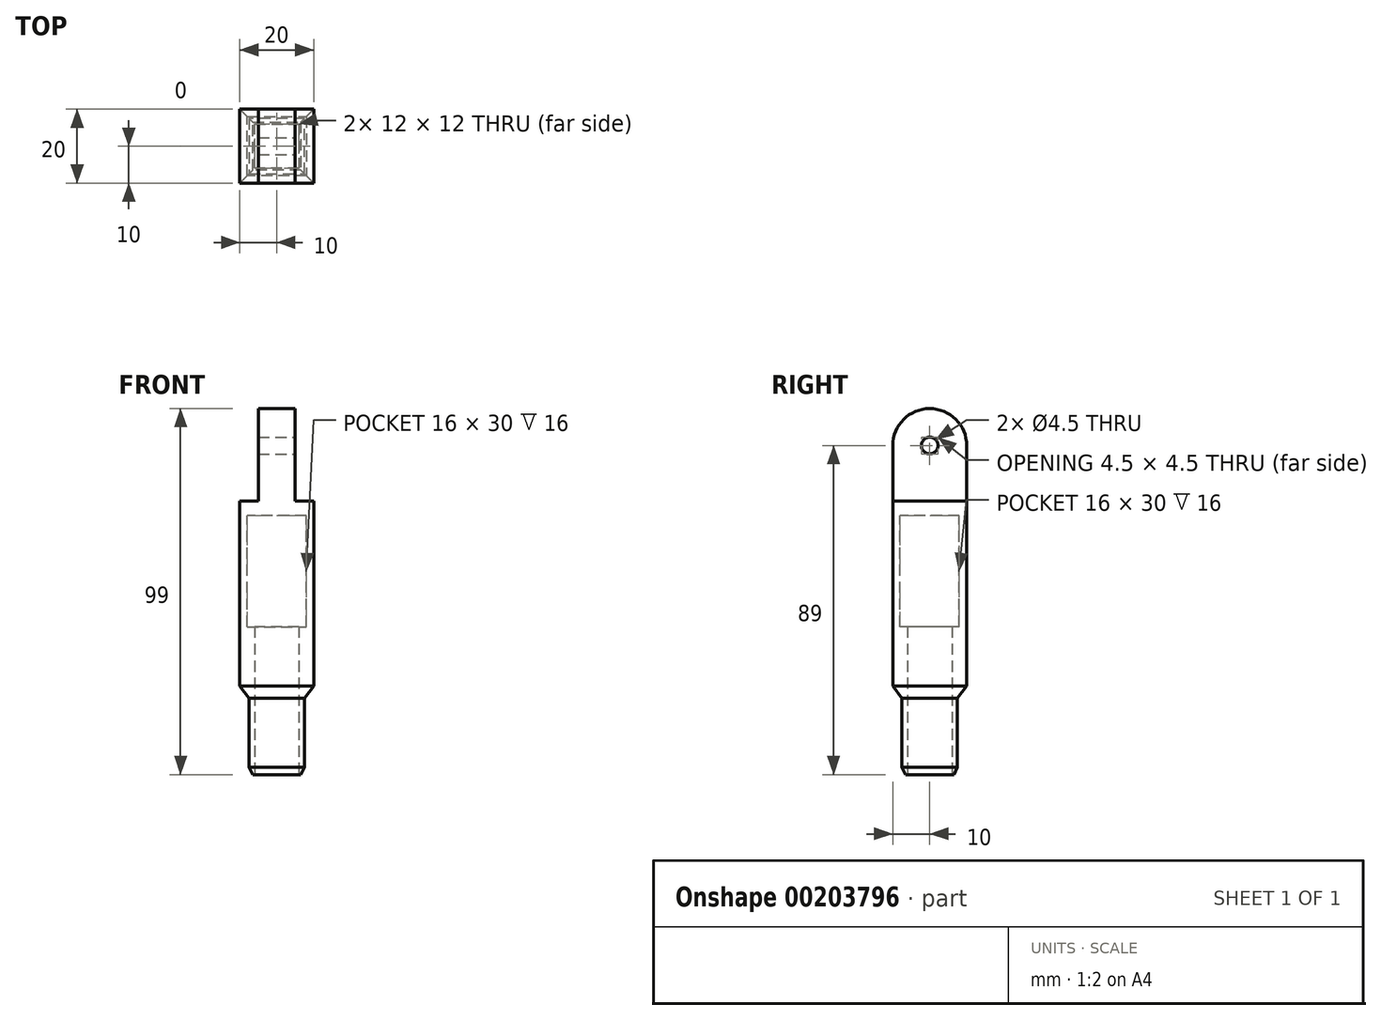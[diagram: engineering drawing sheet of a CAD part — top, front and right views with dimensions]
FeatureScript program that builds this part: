
annotation { "Feature Type Name" : "Feature", "Feature Type Description" : "" }
export const myFeature = defineFeature(function(context is Context, id is Id, definition is map)
    precondition{}
    {
        {
            var Q0;
            Q0=qCreatedBy(makeId("Top.planeOp"),FACE);
            var sketch = newSketch(context, id + "F0", { "sketchPlane" : qUnion([Q0])});
            skLineSegment(sketch, "E0.bottom", {"start": v(10, 10) * mm, "end": v(-10, 10) * mm});
            skLineSegment(sketch, "E0.top", {"start": v(10, -10) * mm, "end": v(-10, -10) * mm});
            skLineSegment(sketch, "E0.left", {"start": v(10, 10) * mm, "end": v(10, -10) * mm});
            skLineSegment(sketch, "E0.right", {"start": v(-10, 10) * mm, "end": v(-10, -10) * mm});
            skPoint(sketch, "E0.middle", {"position": v(0, 0) * mm});
            skSolve(sketch);
        }
        {
            var Q0;
            Q0=makeQuery(id+"F0.imprint","IMPRINT",FACE,{"disambiguationData":[TD([[makeQuery(id+"F0.imprint","IMPRINT",EDGE,{"derivedFrom":sQuery(id+"F0.wireOp",EDGE,"E0.bottom")}),1.0]])]});
            extrude(context, id + "F1", {"entities" : qUnion([Q0]), "depth" : 4 * mm});
        }
        {
            var Q0;
            Q0=makeQuery(id+"F1.opExtrude","CAP_FACE",FACE,{"disambiguationData":[OSD([sQuery(id+"F0.wireOp",EDGE,"E0.bottom"),sQuery(id+"F0.wireOp",EDGE,"E0.top"),sQuery(id+"F0.wireOp",EDGE,"E0.left"),sQuery(id+"F0.wireOp",EDGE,"E0.right")])],"isStart":false});
            var sketch = newSketch(context, id + "F2", { "sketchPlane" : qUnion([Q0])});
            skLineSegment(sketch, "E1.bottom", {"start": v(5, -10) * mm, "end": v(-5, -10) * mm});
            skLineSegment(sketch, "E1.top", {"start": v(5, 10) * mm, "end": v(-5, 10) * mm});
            skLineSegment(sketch, "E1.left", {"start": v(5, -10) * mm, "end": v(5, 10) * mm});
            skLineSegment(sketch, "E1.right", {"start": v(-5, -10) * mm, "end": v(-5, 10) * mm});
            skPoint(sketch, "E1.middle", {"position": v(0, 0) * mm});
            skSolve(sketch);
        }
        {
            var Q0;
            Q0=makeQuery(id+"F2.imprint","IMPRINT",FACE,{"disambiguationData":[TD([[makeQuery(id+"F2.imprint","IMPRINT",EDGE,{"derivedFrom":sQuery(id+"F2.wireOp",EDGE,"E1.bottom")}),-1.0]])]});
            extrude(context, id + "F3", {"entities" : qUnion([Q0]), "operationType" : NewBodyOperationType.ADD, "depth" : 25 * mm});
        }
        {
            var Q0;
            Q0=makeQuery(id+"F3.opExtrude","SWEPT_FACE",FACE,{"disambiguationData":[OSD([sQuery(id+"F2.wireOp",EDGE,"E1.left")])]});
            var sketch = newSketch(context, id + "F4", { "sketchPlane" : qUnion([Q0])});
            skLineSegment(sketch, "E2", {"start": v(0, 29) * mm, "end": v(0, 19) * mm, "construction": true});
            skPoint(sketch, "E2.endSnap0", {"position": v(0, 29) * mm});
            skArc(sketch, "E3", {"start": v(10, 19) * mm, "mid": v(0, 29) * mm, "end": v(-10, 19) * mm});
            skCircle(sketch, "E4", {"center": v(0, 19) * mm, "radius": 2.25 * mm});
            skSolve(sketch);
        }
        {
            var Q0;
            {var subQ0=sQuery(id+"F4.wireOp",EDGE,"E3");var subQ1=sQuery(id+"F2.wireOp",EDGE,"E1.left");var subQ4=makeQuery(id+"F3.opExtrude","CAP_EDGE",EDGE,{"disambiguationData":[OSD([subQ1])],"isStart":false});var subQ5=makeQuery(id+"F4.imprint","INTERSECT",VERTEX,{"derivedFrom":[subQ4,subQ0]});Q0=makeQuery(id+"F4.imprint","IMPRINT",FACE,{"disambiguationData":[TD([[makeQuery(id+"F4.imprint","IMPRINT",EDGE,{"disambiguationData":[TD([[subQ5,-1.0]])],"derivedFrom":subQ0}),-1.0]])]});}
            var Q1;
            {var subQ0=sQuery(id+"F4.wireOp",EDGE,"E3");var subQ1=sQuery(id+"F2.wireOp",EDGE,"E1.left");var subQ4=makeQuery(id+"F3.opExtrude","CAP_EDGE",EDGE,{"disambiguationData":[OSD([subQ1])],"isStart":false});var subQ5=makeQuery(id+"F4.imprint","INTERSECT",VERTEX,{"derivedFrom":[subQ4,subQ0]});Q1=makeQuery(id+"F4.imprint","IMPRINT",FACE,{"disambiguationData":[TD([[makeQuery(id+"F4.imprint","IMPRINT",EDGE,{"disambiguationData":[TD([[subQ5,1.0]])],"derivedFrom":subQ0}),-1.0]])]});}
            var Q2;
            Q2=makeQuery(id+"F4.imprint","IMPRINT",FACE,{"disambiguationData":[TD([[makeQuery(id+"F4.imprint","IMPRINT",EDGE,{"derivedFrom":sQuery(id+"F4.wireOp",EDGE,"E4")}),1.0]])]});
            extrude(context, id + "F5", {"entities" : qUnion([Q0, Q1, Q2]), "operationType" : NewBodyOperationType.REMOVE, "endBound" : BoundingType.THROUGH_ALL, "oppositeDirection" : true, "depth" : 25 * mm});
        }
        {
            var Q0;
            Q0=makeQuery(id+"F1.opExtrude","CAP_FACE",FACE,{"disambiguationData":[OSD([sQuery(id+"F0.wireOp",EDGE,"E0.bottom"),sQuery(id+"F0.wireOp",EDGE,"E0.top"),sQuery(id+"F0.wireOp",EDGE,"E0.left"),sQuery(id+"F0.wireOp",EDGE,"E0.right")])],"isStart":true});
            var sketch = newSketch(context, id + "F6", { "sketchPlane" : qUnion([Q0])});
            skLineSegment(sketch, "E5.bottom", {"start": v(-10, -10) * mm, "end": v(10, -10) * mm});
            skLineSegment(sketch, "E5.top", {"start": v(-10, 10) * mm, "end": v(10, 10) * mm});
            skLineSegment(sketch, "E5.left", {"start": v(-10, -10) * mm, "end": v(-10, 10) * mm});
            skLineSegment(sketch, "E5.right", {"start": v(10, -10) * mm, "end": v(10, 10) * mm});
            skPoint(sketch, "E5.middle", {"position": v(0, 0) * mm});
            skLineSegment(sketch, "E6.0", {"start": v(8, 8) * mm, "end": v(-8, 8) * mm});
            skLineSegment(sketch, "E6.1", {"start": v(8, -8) * mm, "end": v(8, 8) * mm});
            skLineSegment(sketch, "E6.2", {"start": v(-8, -8) * mm, "end": v(8, -8) * mm});
            skLineSegment(sketch, "E6.3", {"start": v(-8, 8) * mm, "end": v(-8, -8) * mm});
            skSolve(sketch);
        }
        {
            var Q0;
            Q0=makeQuery(id+"F6.imprint","IMPRINT",FACE,{"disambiguationData":[TD([[makeQuery(id+"F6.imprint","IMPRINT",EDGE,{"derivedFrom":sQuery(id+"F6.wireOp",EDGE,"E5.bottom")}),-1.0]])]});
            extrude(context, id + "F7", {"entities" : qUnion([Q0]), "operationType" : NewBodyOperationType.ADD, "depth" : 50 * mm});
        }
        {
            var Q0;
            Q0=makeQuery(id+"F7.opExtrude","CAP_FACE",FACE,{"disambiguationData":[OSD([sQuery(id+"F6.wireOp",EDGE,"E5.bottom"),sQuery(id+"F6.wireOp",EDGE,"E5.top"),sQuery(id+"F6.wireOp",EDGE,"E5.left"),sQuery(id+"F6.wireOp",EDGE,"E5.right"),sQuery(id+"F6.wireOp",EDGE,"E6.0"),sQuery(id+"F6.wireOp",EDGE,"E6.1"),sQuery(id+"F6.wireOp",EDGE,"E6.2"),sQuery(id+"F6.wireOp",EDGE,"E6.3")])],"isStart":false});
            var sketch = newSketch(context, id + "F8", { "sketchPlane" : qUnion([Q0])});
            skLineSegment(sketch, "E7.bottom", {"start": v(-8, 8) * mm, "end": v(8, 8) * mm});
            skLineSegment(sketch, "E7.top", {"start": v(-8, -8) * mm, "end": v(8, -8) * mm});
            skLineSegment(sketch, "E7.left", {"start": v(-8, 8) * mm, "end": v(-8, -8) * mm});
            skLineSegment(sketch, "E7.right", {"start": v(8, 8) * mm, "end": v(8, -8) * mm});
            skPoint(sketch, "E7.middle", {"position": v(0, 0) * mm});
            skLineSegment(sketch, "E8.0", {"start": v(6, 6) * mm, "end": v(-6, 6) * mm});
            skLineSegment(sketch, "E8.1", {"start": v(6, -6) * mm, "end": v(6, 6) * mm});
            skLineSegment(sketch, "E8.2", {"start": v(-6, -6) * mm, "end": v(6, -6) * mm});
            skLineSegment(sketch, "E8.3", {"start": v(-6, 6) * mm, "end": v(-6, -6) * mm});
            skSolve(sketch);
        }
        {
            var Q0;
            Q0=makeQuery(id+"F8.imprint","IMPRINT",FACE,{"disambiguationData":[TD([[makeQuery(id+"F8.imprint","IMPRINT",EDGE,{"derivedFrom":sQuery(id+"F8.wireOp",EDGE,"E7.bottom")}),1.0]])]});
            extrude(context, id + "F9", {"entities" : qUnion([Q0]), "operationType" : NewBodyOperationType.ADD, "oppositeDirection" : true, "depth" : 20 * mm});
        }
        {
            var Q0;
            Q0=makeQuery(id+"F9.boolean.opBoolean","MERGE",FACE,{"derivedFrom":[makeQuery(id+"F7.opExtrude","CAP_FACE",FACE,{"disambiguationData":[OSD([sQuery(id+"F6.wireOp",EDGE,"E5.bottom"),sQuery(id+"F6.wireOp",EDGE,"E5.top"),sQuery(id+"F6.wireOp",EDGE,"E5.left"),sQuery(id+"F6.wireOp",EDGE,"E5.right"),sQuery(id+"F6.wireOp",EDGE,"E6.0"),sQuery(id+"F6.wireOp",EDGE,"E6.1"),sQuery(id+"F6.wireOp",EDGE,"E6.2"),sQuery(id+"F6.wireOp",EDGE,"E6.3")])],"isStart":false}),makeQuery(id+"F9.opExtrude","CAP_FACE",FACE,{"disambiguationData":[OSD([sQuery(id+"F8.wireOp",EDGE,"E7.bottom"),sQuery(id+"F8.wireOp",EDGE,"E7.top"),sQuery(id+"F8.wireOp",EDGE,"E7.left"),sQuery(id+"F8.wireOp",EDGE,"E7.right"),sQuery(id+"F8.wireOp",EDGE,"E8.0"),sQuery(id+"F8.wireOp",EDGE,"E8.1"),sQuery(id+"F8.wireOp",EDGE,"E8.2"),sQuery(id+"F8.wireOp",EDGE,"E8.3")])],"isStart":true})]});
            var sketch = newSketch(context, id + "F10", { "sketchPlane" : qUnion([Q0])});
            skLineSegment(sketch, "E9.bottom", {"start": v(-6, -6) * mm, "end": v(6, -6) * mm});
            skLineSegment(sketch, "E9.top", {"start": v(-6, 6) * mm, "end": v(6, 6) * mm});
            skLineSegment(sketch, "E9.left", {"start": v(-6, -6) * mm, "end": v(-6, 6) * mm});
            skLineSegment(sketch, "E9.right", {"start": v(6, -6) * mm, "end": v(6, 6) * mm});
            skPoint(sketch, "E9.middle", {"position": v(0, 0) * mm});
            skLineSegment(sketch, "E10.0", {"start": v(-7.5, 7.5) * mm, "end": v(7.5, 7.5) * mm});
            skLineSegment(sketch, "E10.1", {"start": v(-7.5, -7.5) * mm, "end": v(-7.5, 7.5) * mm});
            skLineSegment(sketch, "E10.2", {"start": v(-7.5, -7.5) * mm, "end": v(7.5, -7.5) * mm});
            skLineSegment(sketch, "E10.3", {"start": v(7.5, -7.5) * mm, "end": v(7.5, 7.5) * mm});
            skSolve(sketch);
        }
        {
            var Q0;
            Q0=makeQuery(id+"F10.imprint","IMPRINT",FACE,{"disambiguationData":[TD([[makeQuery(id+"F10.imprint","IMPRINT",EDGE,{"derivedFrom":sQuery(id+"F10.wireOp",EDGE,"E9.bottom")}),-1.0]])]});
            extrude(context, id + "F11", {"entities" : qUnion([Q0]), "operationType" : NewBodyOperationType.ADD, "depth" : 20 * mm});
        }
        {
            var Q0;
            Q0=makeQuery(id+"F7.opExtrude","CAP_EDGE",EDGE,{"disambiguationData":[OSD([sQuery(id+"F6.wireOp",EDGE,"E5.top")])],"isStart":false});
            var Q1;
            Q1=makeQuery(id+"F7.opExtrude","CAP_EDGE",EDGE,{"disambiguationData":[OSD([sQuery(id+"F6.wireOp",EDGE,"E5.right")])],"isStart":false});
            var Q2;
            Q2=makeQuery(id+"F7.opExtrude","CAP_EDGE",EDGE,{"disambiguationData":[OSD([sQuery(id+"F6.wireOp",EDGE,"E5.left")])],"isStart":false});
            var Q3;
            Q3=makeQuery(id+"F7.opExtrude","CAP_EDGE",EDGE,{"disambiguationData":[OSD([sQuery(id+"F6.wireOp",EDGE,"E5.bottom")])],"isStart":false});
            chamfer(context, id + "F12", {"entities" : qUnion([Q0, Q1, Q2, Q3]), "chamferType" : ChamferType.TWO_OFFSETS, "width1" : 3 * mm, "oppositeDirection" : false, "width2" : 4 * mm, "tangentPropagation" : true});
        }
        {
            var Q0;
            Q0=makeQuery(id+"F11.opExtrude","CAP_EDGE",EDGE,{"disambiguationData":[OSD([sQuery(id+"F10.wireOp",EDGE,"E10.0")])],"isStart":false});
            var Q1;
            Q1=makeQuery(id+"F11.opExtrude","CAP_EDGE",EDGE,{"disambiguationData":[OSD([sQuery(id+"F10.wireOp",EDGE,"E10.3")])],"isStart":false});
            var Q2;
            Q2=makeQuery(id+"F11.opExtrude","CAP_EDGE",EDGE,{"disambiguationData":[OSD([sQuery(id+"F10.wireOp",EDGE,"E10.1")])],"isStart":false});
            var Q3;
            Q3=makeQuery(id+"F11.opExtrude","CAP_EDGE",EDGE,{"disambiguationData":[OSD([sQuery(id+"F10.wireOp",EDGE,"E10.2")])],"isStart":false});
            chamfer(context, id + "F13", {"entities" : qUnion([Q0, Q1, Q2, Q3]), "chamferType" : ChamferType.TWO_OFFSETS, "width1" : 2 * mm, "oppositeDirection" : false, "width2" : 1 * mm, "tangentPropagation" : true});
        }
        {
            var Q0;
            Q0=makeQuery(id+"F1.opExtrude","SWEPT_BODY",BODY,{"disambiguationData":[OSD([sQuery(id+"F0.wireOp",EDGE,"E0.bottom"),sQuery(id+"F0.wireOp",EDGE,"E0.top"),sQuery(id+"F0.wireOp",EDGE,"E0.left"),sQuery(id+"F0.wireOp",EDGE,"E0.right")])]});
            transform(context, id + "F14", {"entities" : qUnion([Q0]), "transformType" : TransformType.TRANSLATION_3D, "dx" : 0 * mm, "dy" : 0 * mm, "dz" : 0 * mm, "makeCopy" : true});
        }
    });
